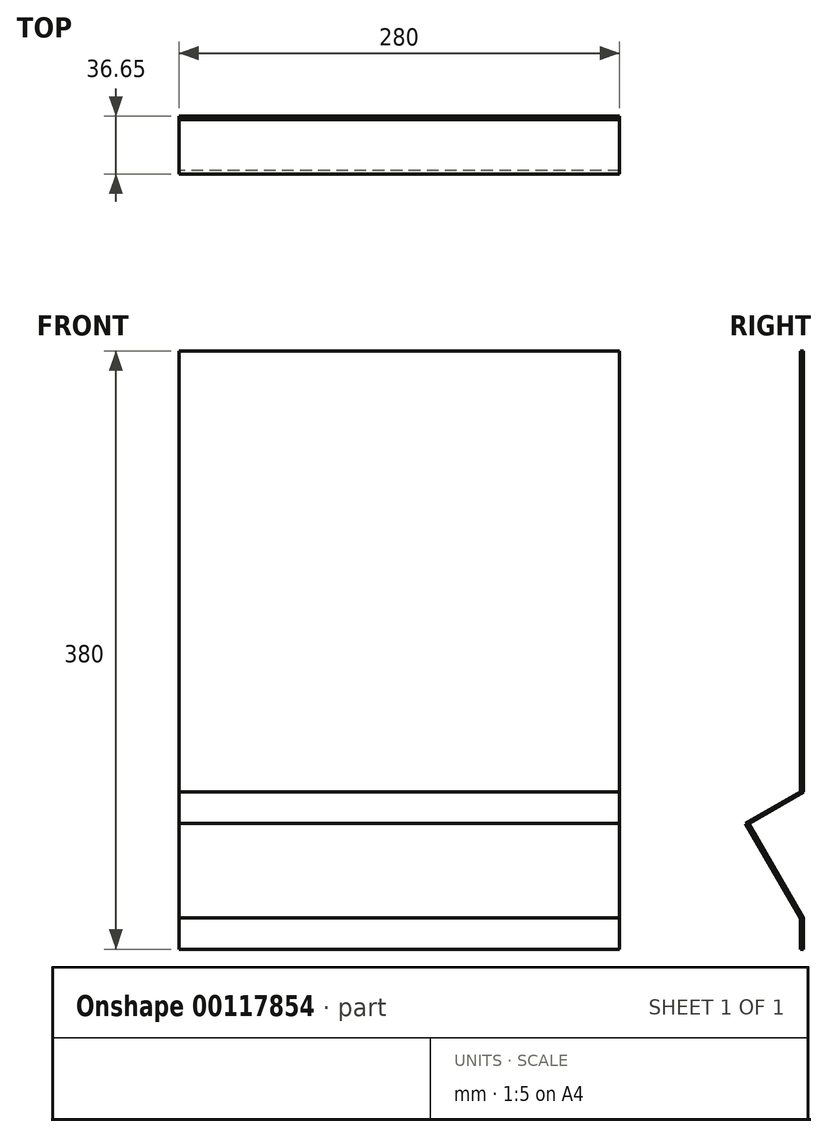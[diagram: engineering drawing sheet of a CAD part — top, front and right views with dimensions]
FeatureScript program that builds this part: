
annotation { "Feature Type Name" : "Feature", "Feature Type Description" : "" }
export const myFeature = defineFeature(function(context is Context, id is Id, definition is map)
    precondition{}
    {
        {
            var Q0;
            Q0=qCreatedBy(makeId("Right.planeOp"),FACE);
            var sketch = newSketch(context, id + "F0", { "sketchPlane" : qUnion([Q0])});
            skLineSegment(sketch, "E0", {"start": v(-174.1, 371.83) * mm, "end": v(-174.1, 391.83) * mm});
            skLineSegment(sketch, "E1", {"start": v(-174.1, 391.83) * mm, "end": v(-208.74, 451.83) * mm});
            skLineSegment(sketch, "E2", {"start": v(-208.74, 451.83) * mm, "end": v(-174.1, 471.83) * mm});
            skLineSegment(sketch, "E3", {"start": v(-174.1, 471.83) * mm, "end": v(-174.1, 751.83) * mm});
            skLineSegment(sketch, "E4", {"start": v(-172.1, 371.83) * mm, "end": v(-172.1, 391.83) * mm});
            skLineSegment(sketch, "E5", {"start": v(-172.1, 391.83) * mm, "end": v(-206.74, 451.83) * mm});
            skLineSegment(sketch, "E6", {"start": v(-206.74, 451.83) * mm, "end": v(-172.1, 471.83) * mm});
            skLineSegment(sketch, "E7", {"start": v(-172.1, 471.83) * mm, "end": v(-172.1, 751.83) * mm});
            skLineSegment(sketch, "E8", {"start": v(-174.1, 751.83) * mm, "end": v(-172.1, 751.83) * mm});
            skLineSegment(sketch, "E9", {"start": v(-174.1, 371.83) * mm, "end": v(-172.1, 371.83) * mm});
            skSolve(sketch);
        }
        {
            var Q0;
            Q0 = qSketchRegion(id + "F0", true);
            extrude(context, id + "F1", {"entities" : qUnion([Q0]), "depth" : 280 * mm});
        }
    });
